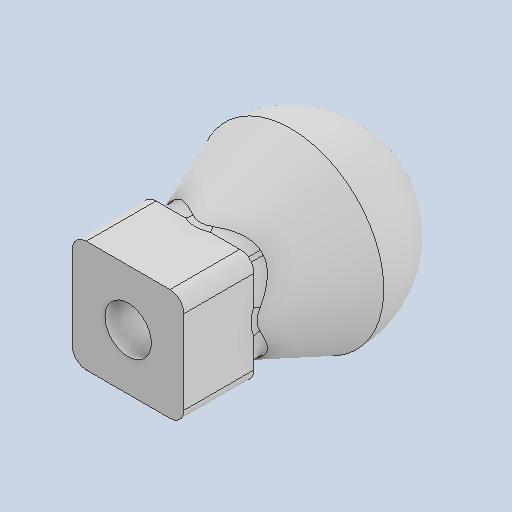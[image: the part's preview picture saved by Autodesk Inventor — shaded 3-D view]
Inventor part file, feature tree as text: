
AUTODESK INVENTOR PART (.ipt)
format: ipt  version: 2024.3 (Build 283343000, 343)  size: 380,416 bytes
history: native  units: mm
features: sketch x2, other x1, revolve x1, extrude x1, fillet x1
ambient origin geometry x8: Origin, YZ Plane, XZ Plane, XY Plane, X Axis, Y Axis, Z Axis, Center Point
bodies: Body1 (feature_tree)
feature tree (6):
  other  "ソリッド1"
  revolve  "回転1"
  extrude  "押し出し2"  Depth=20.0mm
  fillet  "フィレット1"  [1 undecoded]
  sketch  "スケッチ4"
  sketch  "スケッチ5"
note: 1 required parameter value undecoded (feature->parameter linkage not recoverable at this tier; creation-order binding heuristic only, values carry confidence <= 0.55)
